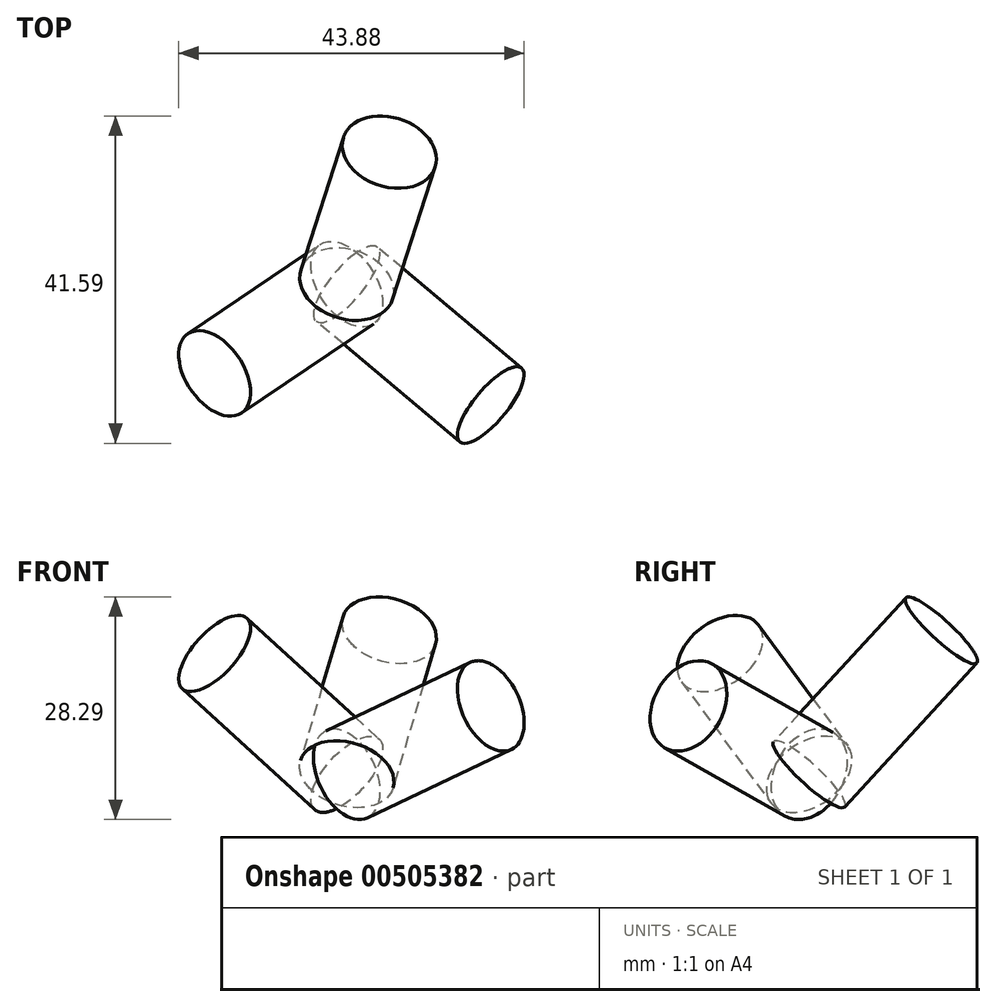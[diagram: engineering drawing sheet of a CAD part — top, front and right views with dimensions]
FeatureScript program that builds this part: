
annotation { "Feature Type Name" : "Feature", "Feature Type Description" : "" }
export const myFeature = defineFeature(function(context is Context, id is Id, definition is map)
    precondition{}
    {
        {
            var Q0;
            Q0=qCreatedBy(makeId("Right.planeOp"),FACE);
            var sketch = newSketch(context, id + "F0", { "sketchPlane" : qUnion([Q0])});
            skCircle(sketch, "E0", {"center": v(0, 0) * mm, "radius": 6.12 * mm});
            skSolve(sketch);
        }
        {
            var Q0;
            Q0=makeQuery(id+"F0.imprint","IMPRINT",FACE,{"disambiguationData":[TD([[makeQuery(id+"F0.imprint","IMPRINT",EDGE,{"derivedFrom":sQuery(id+"F0.wireOp",EDGE,"E0")}),1.0]])]});
            extrude(context, id + "F1", {"entities" : qUnion([Q0]), "depth" : 25.4 * mm});
        }
        {
            var Q0;
            Q0=qCreatedBy(makeId("Front.planeOp"),FACE);
            var sketch = newSketch(context, id + "F2", { "sketchPlane" : qUnion([Q0])});
            skCircle(sketch, "E1", {"center": v(0, 0) * mm, "radius": 6.08 * mm});
            skSolve(sketch);
        }
        {
            var Q0;
            Q0 = qSketchRegion(id + "F2", true);
            extrude(context, id + "F3", {"entities" : qUnion([Q0]), "oppositeDirection" : true, "depth" : 25.4 * mm});
        }
        {
            var Q0;
            Q0=qCreatedBy(makeId("Top.planeOp"),FACE);
            var sketch = newSketch(context, id + "F4", { "sketchPlane" : qUnion([Q0])});
            skCircle(sketch, "E2", {"center": v(0, 0) * mm, "radius": 6.11 * mm});
            skSolve(sketch);
        }
        {
            var Q0;
            Q0 = qSketchRegion(id + "F4", true);
            extrude(context, id + "F5", {"entities" : qUnion([Q0]), "depth" : 25.4 * mm});
        }
        {
            var Q0;
            Q0=makeQuery(id+"F3.opExtrude","SWEPT_BODY",BODY,{"disambiguationData":[OSD([sQuery(id+"F2.wireOp",EDGE,"E1")])]});
            var Q1;
            Q1=makeQuery(id+"F5.opExtrude","SWEPT_BODY",BODY,{"disambiguationData":[OSD([sQuery(id+"F4.wireOp",EDGE,"E2")])]});
            var Q2;
            Q2=makeQuery(id+"F1.opExtrude","SWEPT_BODY",BODY,{"disambiguationData":[OSD([sQuery(id+"F0.wireOp",EDGE,"E0")])]});
            var Q3;
            Q3=makeQuery(id+"F5.opExtrude","SWEPT_FACE",FACE,{"disambiguationData":[OSD([sQuery(id+"F4.wireOp",EDGE,"E2")])]});
            transform(context, id + "F6", {"entities" : qUnion([Q0, Q1, Q2]), "transformType" : TransformType.ROTATION, "transformAxis" : qUnion([Q3]), "angle" : 50 * degree, "oppositeDirection" : true, "makeCopy" : false});
        }
        {
            var Q0;
            Q0=makeQuery(id+"F3.opExtrude","SWEPT_BODY",BODY,{"disambiguationData":[OSD([sQuery(id+"F2.wireOp",EDGE,"E1")])]});
            var Q1;
            Q1=makeQuery(id+"F5.opExtrude","SWEPT_BODY",BODY,{"disambiguationData":[OSD([sQuery(id+"F4.wireOp",EDGE,"E2")])]});
            var Q2;
            Q2=makeQuery(id+"F1.opExtrude","SWEPT_BODY",BODY,{"disambiguationData":[OSD([sQuery(id+"F0.wireOp",EDGE,"E0")])]});
            var Q3;
            Q3=makeQuery(id+"F1.opExtrude","SWEPT_FACE",FACE,{"disambiguationData":[OSD([sQuery(id+"F0.wireOp",EDGE,"E0")])]});
            transform(context, id + "F7", {"entities" : qUnion([Q0, Q1, Q2]), "transformType" : TransformType.ROTATION, "transformAxis" : qUnion([Q3]), "angle" : 70 * degree, "oppositeDirection" : true, "makeCopy" : false});
        }
        {
            var Q0;
            Q0=makeQuery(id+"F5.opExtrude","SWEPT_BODY",BODY,{"disambiguationData":[OSD([sQuery(id+"F4.wireOp",EDGE,"E2")])]});
            var Q1;
            Q1=makeQuery(id+"F1.opExtrude","SWEPT_BODY",BODY,{"disambiguationData":[OSD([sQuery(id+"F0.wireOp",EDGE,"E0")])]});
            var Q2;
            Q2=makeQuery(id+"F3.opExtrude","SWEPT_BODY",BODY,{"disambiguationData":[OSD([sQuery(id+"F2.wireOp",EDGE,"E1")])]});
            var Q3;
            Q3=makeQuery(id+"F5.opExtrude","SWEPT_FACE",FACE,{"disambiguationData":[OSD([sQuery(id+"F4.wireOp",EDGE,"E2")])]});
            transform(context, id + "F8", {"entities" : qUnion([Q0, Q1, Q2]), "transformType" : TransformType.ROTATION, "transformAxis" : qUnion([Q3]), "angle" : 50 * degree, "oppositeDirection" : true, "makeCopy" : false});
        }
    });
